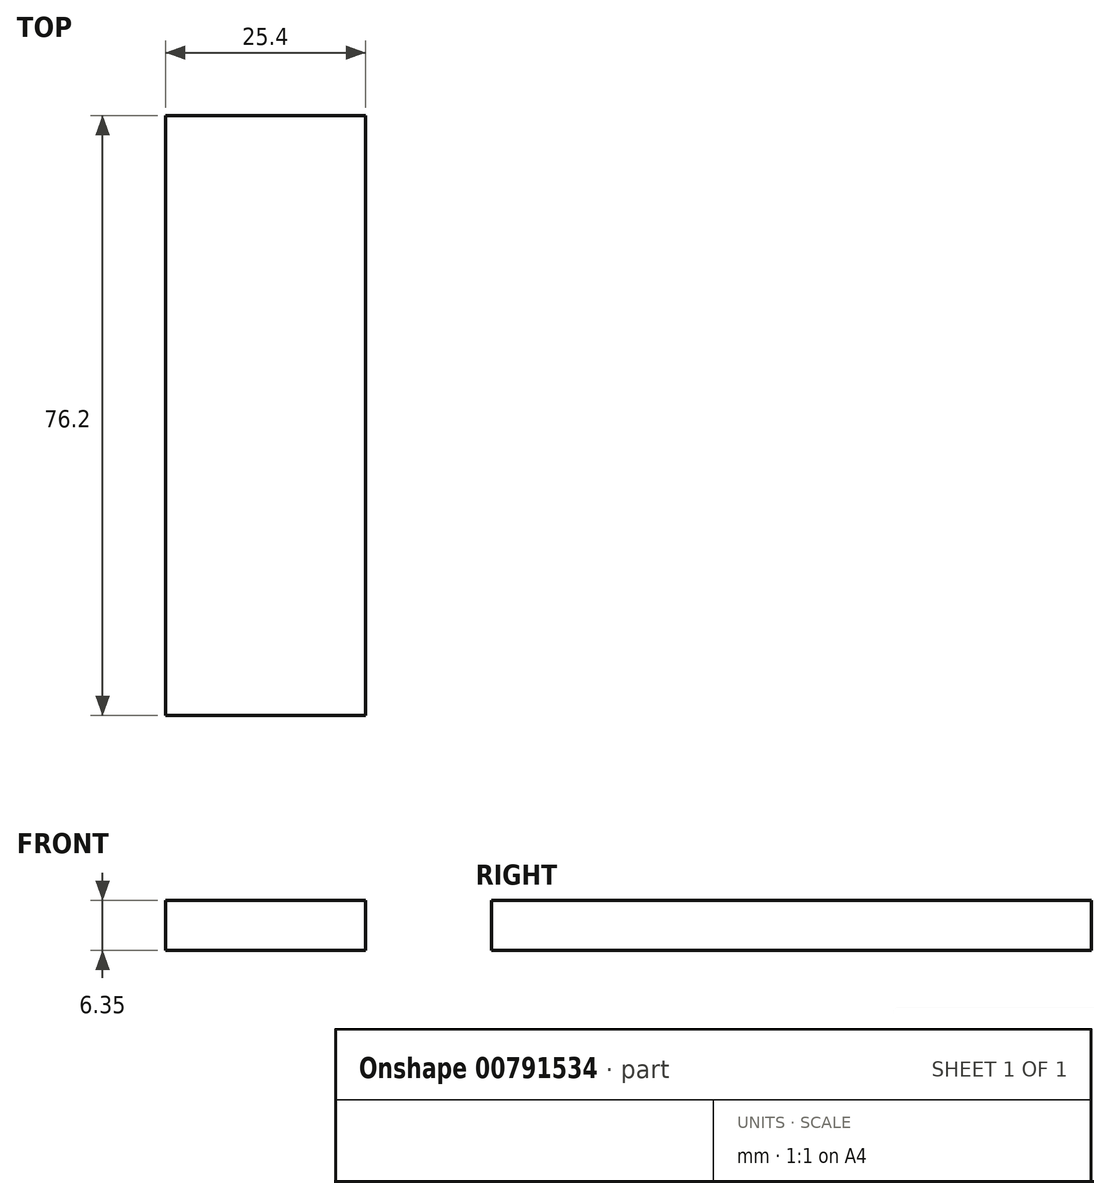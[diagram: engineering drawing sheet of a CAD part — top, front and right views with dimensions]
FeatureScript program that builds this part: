
annotation { "Feature Type Name" : "Feature", "Feature Type Description" : "" }
export const myFeature = defineFeature(function(context is Context, id is Id, definition is map)
    precondition{}
    {
        {
            var Q0;
            Q0=qCreatedBy(makeId("Front.planeOp"),FACE);
            var sketch = newSketch(context, id + "F0", { "sketchPlane" : qUnion([Q0])});
            skLineSegment(sketch, "E0", {"start": v(1.48, 0) * mm, "end": v(26.88, 0) * mm});
            skLineSegment(sketch, "E1", {"start": v(26.88, 0) * mm, "end": v(26.88, -6.35) * mm});
            skLineSegment(sketch, "E2", {"start": v(26.88, -6.35) * mm, "end": v(1.48, -6.35) * mm});
            skLineSegment(sketch, "E3", {"start": v(1.48, -6.35) * mm, "end": v(1.48, 0) * mm});
            skSolve(sketch);
        }
        {
            var Q0;
            Q0 = qSketchRegion(id + "F0", true);
            extrude(context, id + "F1", {"entities" : qUnion([Q0]), "depth" : 76.2 * mm, "offsetDistance" : 25.4 * mm});
        }
    });
